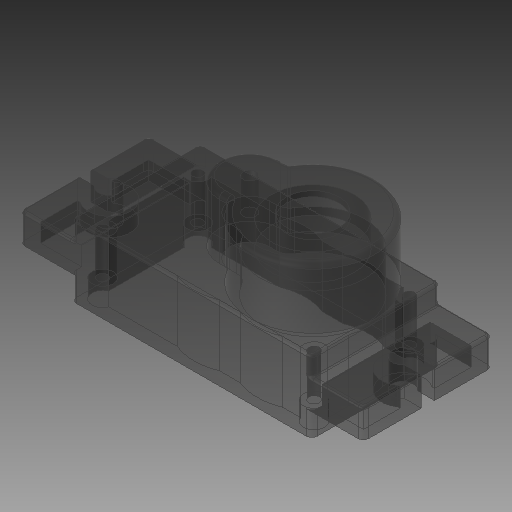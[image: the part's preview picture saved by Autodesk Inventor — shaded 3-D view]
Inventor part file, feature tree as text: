
AUTODESK INVENTOR PART (.ipt)
format: ipt  version: 2019 (Build 230136000, 136)  size: 455,680 bytes
history: native  units: mm
features: extrude x12, sketch x7, projected_geometry x2, fillet x1, shell x1
ambient origin geometry x8: Origin, YZ Plane, XZ Plane, XY Plane, X Axis, Y Axis, Z Axis, Center Point
bodies: Solid1 (feature_tree)
feature tree (23):
  extrude  "Extrusion1"  Depth=22.75mm
  extrude  "Extrusion2"  Depth=32.5mm
  extrude  "Extrusion3"  Depth=12.2mm TaperAngle=0.0deg
  fillet  "Fillet1"  Radius=11.8mm
  shell  "Shell1"  Thickness=6.0mm
  sketch  "Sketch4"  dims[d9=5.75mm d10=5.975mm d11=2.875mm]
  extrude  "Extrusion4"  Depth=2.875mm
  extrude  "Extrusion5"  Depth=1.25mm
  sketch  "Sketch5"  dims[d12=5.75mm d13=0.0mm d14=2.0mm d15=1.25mm]
  extrude  "Extrusion6"  Depth=1.25mm
  extrude  "Extrusion7"  Depth=0.5mm
  extrude  "Extrusion8"  Depth=1.0mm
  extrude  "Extrusion9"  Depth=1.0mm
  extrude  "Extrusion10"  Depth=1.25mm
  extrude  "Extrusion11"  Depth=1.75mm
  extrude  "Extrusion12"  Depth=1.75mm
  sketch  "Sketch1"  dims[d0=22.75mm d1=6.8mm]
  sketch  "Sketch2"  dims[d2=2.75mm d3=32.5mm]
  sketch  "Sketch3"  dims[d4=2.25mm d5=12.2mm d6=0.0mm d7=11.8mm d8=6.0mm]
  projected_geometry  "Projected Loop1"
  projected_geometry  "Projected Loop2"
  sketch  "Sketch6"  dims[d16=2.0mm d17=1.25mm d18=27.75mm]
  sketch  "Sketch7"  dims[d19=5.75mm d20=0.0mm d21=0.5mm d22=0.25mm d23=0.1mm d24=1.0mm d25=1.0mm d26=1.25mm d27=2.0mm d28=20.0mm d29=9.0mm d30=0.0mm d31=0.0mm d32=5.75mm d33=0.0mm d34=5.0mm d35=7.8mm d36=2.0mm d37=0.0mm d38=2.0mm d39=0.0mm d40=0.5mm d41=0.0mm d42=1.25mm d43=0.5mm d44=0.0mm d45=10.5mm d46=0.5mm d47=0.0mm d48=10.5mm d49=1.0mm d50=0.5mm d51=0.0mm d52=1.75mm d53=0.0mm]
